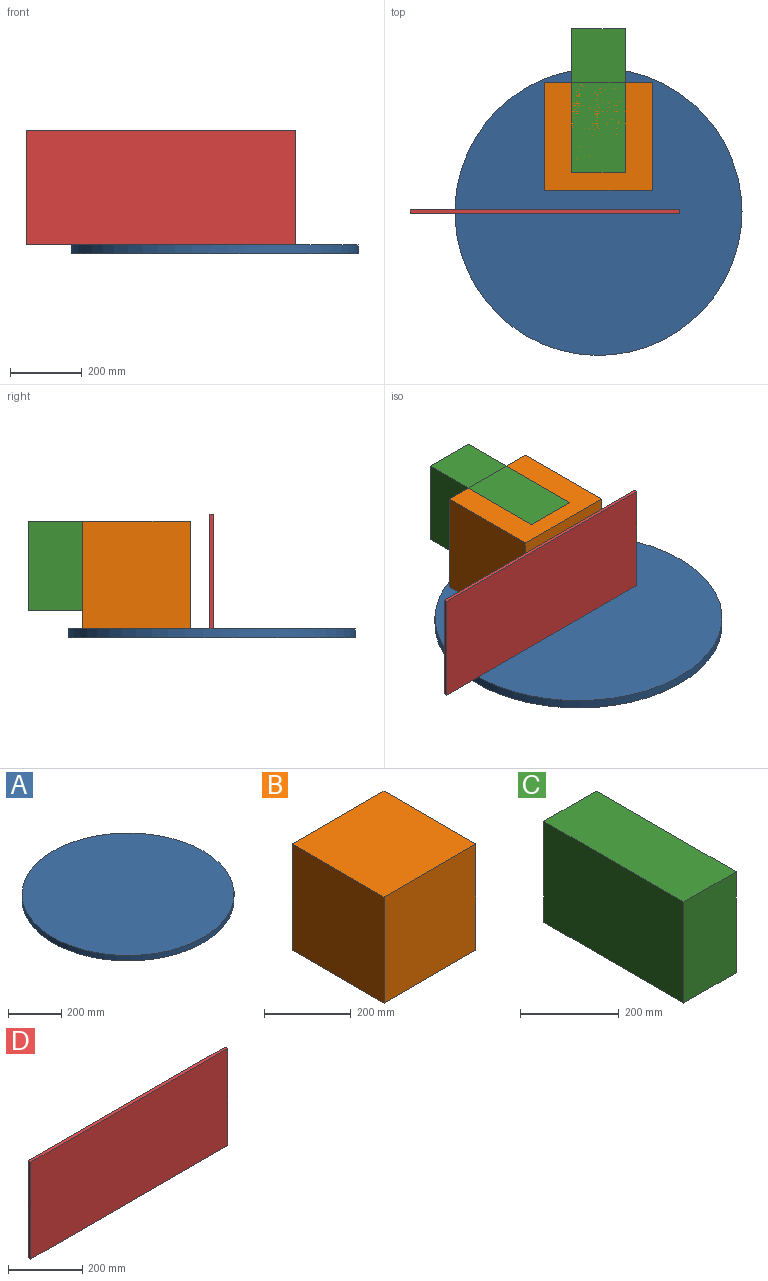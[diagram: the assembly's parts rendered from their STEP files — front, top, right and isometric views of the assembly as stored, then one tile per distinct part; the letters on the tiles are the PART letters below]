
ASSEMBLY  parts=4 mates=3
PART A: 3 faces, bbox 800x800x25 mm
  f0: cylinder r=400mm len=800mm, axis (0,0,-1), area 62831.9mm2, adj f1,f2
  f1: plane 800x800mm, normal (0,0,1), area 502654.8mm2, adj f0
  f2: plane 800x800mm, normal (0,0,-1), area 502654.8mm2, adj f0
PART B: 6 faces, bbox 300x300x300 mm
  f0: plane 300x300mm, normal (-1,0,0), area 90000mm2, adj f1,f3,f4,f5
  f1: plane 300x300mm, normal (0,-1,0), area 90000mm2, adj f0,f2,f4,f5
  f2: plane 300x300mm, normal (1,0,0), area 90000mm2, adj f1,f3,f4,f5
  f3: plane 300x300mm, normal (0,1,0), area 90000mm2, adj f0,f2,f4,f5
  f4: plane 300x300mm, normal (0,0,1), area 90000mm2, adj f0,f1,f2,f3
  f5: plane 300x300mm, normal (0,0,-1), area 90000mm2, adj f0,f1,f2,f3
PART C: 6 faces, bbox 150x400x250 mm
  f0: plane 400x250mm, normal (-1,0,0), area 100000mm2, adj f1,f3,f4,f5
  f1: plane 250x150mm, normal (0,-1,0), area 37500mm2, adj f0,f2,f4,f5
  f2: plane 400x250mm, normal (1,0,0), area 100000mm2, adj f1,f3,f4,f5
  f3: plane 250x150mm, normal (0,1,0), area 37500mm2, adj f0,f2,f4,f5
  f4: plane 400x150mm, normal (0,0,1), area 60000mm2, adj f0,f1,f2,f3
  f5: plane 400x150mm, normal (0,0,-1), area 60000mm2, adj f0,f1,f2,f3
PART D: 6 faces, bbox 750x10x320 mm
  f0: plane 320x10mm, normal (-1,0,0), area 3200mm2, adj f1,f3,f4,f5
  f1: plane 750x320mm, normal (0,-1,0), area 240000mm2, adj f0,f2,f4,f5
  f2: plane 320x10mm, normal (1,0,0), area 3200mm2, adj f1,f3,f4,f5
  f3: plane 750x320mm, normal (0,1,0), area 240000mm2, adj f0,f2,f4,f5
  f4: plane 750x10mm, normal (0,0,1), area 7500mm2, adj f0,f1,f2,f3
  f5: plane 750x10mm, normal (0,0,-1), area 7500mm2, adj f0,f1,f2,f3
PLACE A at identity fixed
PLACE B t=(-150,60,25)mm
PLACE C t=(-75,110,75)mm
PLACE D t=(-525,-5,25)mm
MATE planar A.f0 <-> D.f5  axis (0,0,1) through (0,0,25)mm
MATE planar A.f0 <-> B.f5  axis (0,0,1) through (0,0,25)mm
MATE planar B.f4 <-> C.f4  axis (0,0,1) through (0,260,325)mm
